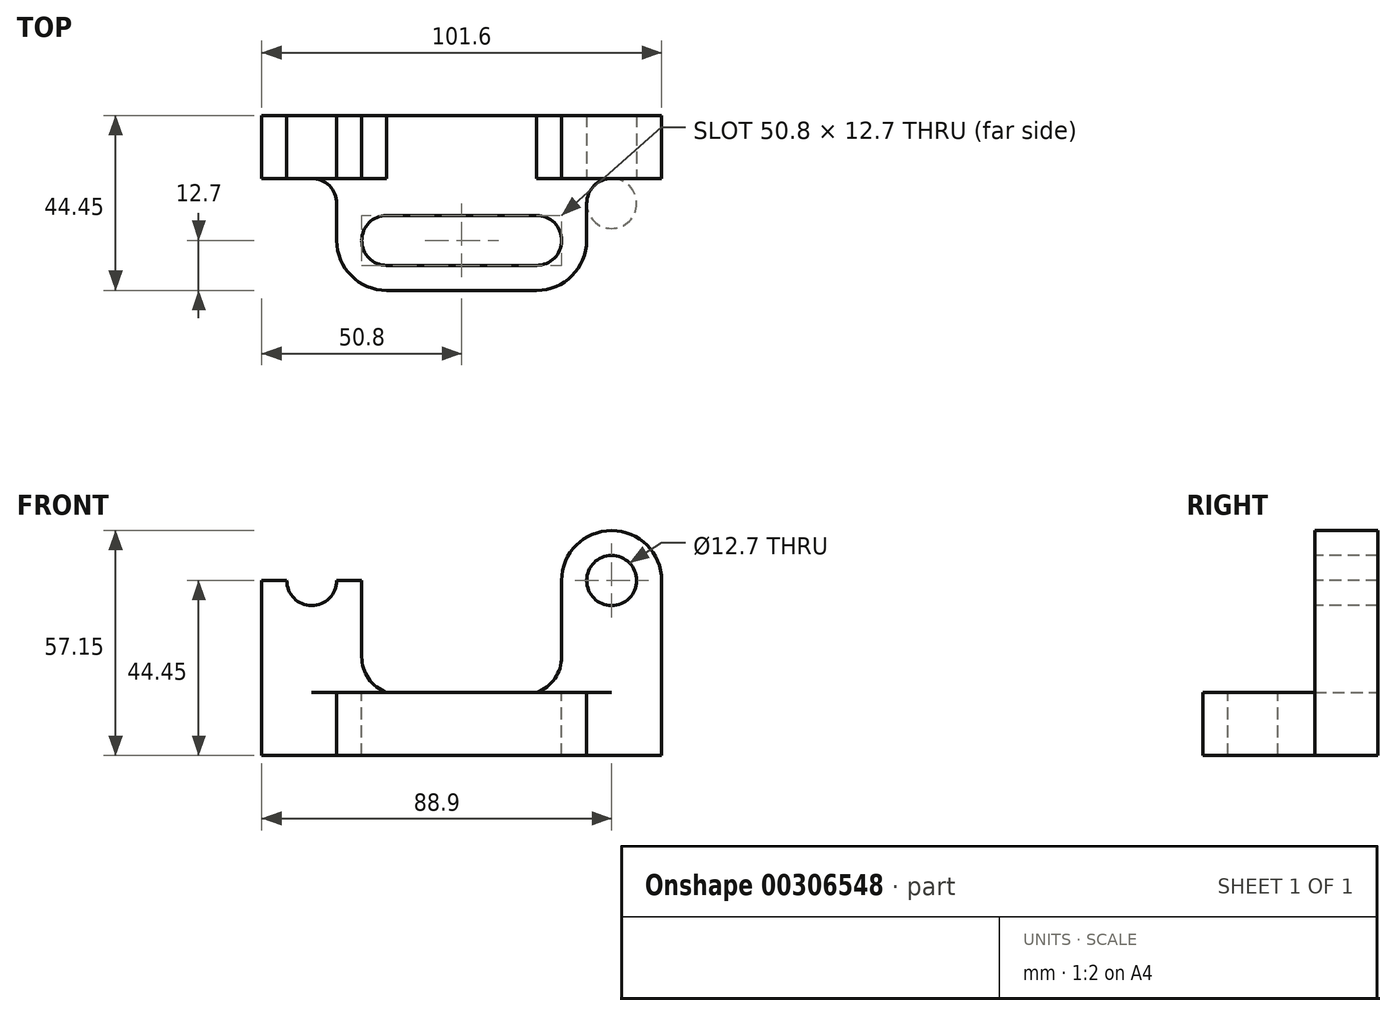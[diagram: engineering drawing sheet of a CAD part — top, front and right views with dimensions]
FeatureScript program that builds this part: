
annotation { "Feature Type Name" : "Feature", "Feature Type Description" : "" }
export const myFeature = defineFeature(function(context is Context, id is Id, definition is map)
    precondition{}
    {
        {
            var Q0;
            Q0=qCreatedBy(makeId("Front.planeOp"),FACE);
            var sketch = newSketch(context, id + "F0", { "sketchPlane" : qUnion([Q0])});
            skLineSegment(sketch, "E0", {"start": v(0, 0) * mm, "end": v(0, 44.45) * mm});
            skLineSegment(sketch, "E1", {"start": v(101.6, 44.45) * mm, "end": v(101.6, 0) * mm});
            skLineSegment(sketch, "E2", {"start": v(101.6, 0) * mm, "end": v(0, 0) * mm});
            skArc(sketch, "E3", {"start": v(0, 44.45) * mm, "mid": v(12.7, 57.15) * mm, "end": v(25.4, 44.45) * mm});
            skArc(sketch, "E4", {"start": v(101.6, 44.45) * mm, "mid": v(88.9, 57.15) * mm, "end": v(76.2, 44.45) * mm});
            skPoint(sketch, "E5.visualSharp", {"position": v(31.75, 16) * mm});
            skPoint(sketch, "E6.visualSharp", {"position": v(69.85, 16) * mm});
            skLineSegment(sketch, "E7", {"start": v(0, 44.45) * mm, "end": v(25.4, 44.45) * mm});
            skLineSegment(sketch, "E8", {"start": v(25.4, 25.07) * mm, "end": v(25.4, 44.45) * mm});
            skLineSegment(sketch, "E9", {"start": v(76.2, 44.45) * mm, "end": v(101.6, 44.45) * mm});
            skLineSegment(sketch, "E10", {"start": v(76.2, 44.45) * mm, "end": v(76.2, 25.07) * mm});
            skLineSegment(sketch, "E11", {"start": v(31.75, 16) * mm, "end": v(69.85, 16) * mm});
            skArc(sketch, "E12", {"start": v(25.4, 25.07) * mm, "mid": v(27.15, 19.54) * mm, "end": v(31.75, 16) * mm});
            skArc(sketch, "E13", {"start": v(76.2, 25.07) * mm, "mid": v(74.45, 19.54) * mm, "end": v(69.85, 16) * mm});
            skSolve(sketch);
        }
        {
            var Q0;
            Q0=makeQuery(id+"F0.imprint","IMPRINT",FACE,{"disambiguationData":[TD([[makeQuery(id+"F0.imprint","IMPRINT",EDGE,{"derivedFrom":sQuery(id+"F0.wireOp",EDGE,"E0")}),-1.0]])]});
            var Q1;
            Q1=makeQuery(id+"F0.imprint","IMPRINT",FACE,{"disambiguationData":[TD([[makeQuery(id+"F0.imprint","IMPRINT",EDGE,{"derivedFrom":sQuery(id+"F0.wireOp",EDGE,"C7aaIfA7-VipN-1Ud3-wAkr-EcyWhxY0K1Mf")}),1.0]])]});
            var Q2;
            Q2=makeQuery(id+"F0.imprint","IMPRINT",FACE,{"disambiguationData":[TD([[makeQuery(id+"F0.imprint","IMPRINT",EDGE,{"derivedFrom":sQuery(id+"F0.wireOp",EDGE,"wvJyilND-zbaq-GOeX-fCs7-xdRXK4oRubfT")}),1.0]])]});
            var Q3;
            Q3=makeQuery(id+"F0.imprint","IMPRINT",FACE,{"disambiguationData":[TD([[makeQuery(id+"F0.imprint","IMPRINT",EDGE,{"derivedFrom":sQuery(id+"F0.wireOp",EDGE,"E3")}),-1.0]])]});
            var Q4;
            Q4=makeQuery(id+"F0.imprint","IMPRINT",FACE,{"disambiguationData":[TD([[makeQuery(id+"F0.imprint","IMPRINT",EDGE,{"derivedFrom":sQuery(id+"F0.wireOp",EDGE,"E4")}),1.0]])]});
            extrude(context, id + "F1", {"entities" : qUnion([Q0, Q1, Q2, Q3, Q4]), "depth" : 16 * mm});
        }
        {
            var Q0;
            Q0=makeQuery(id+"F1.opExtrude","CAP_FACE",FACE,{"disambiguationData":[OSD([sQuery(id+"F0.wireOp",EDGE,"E0"),sQuery(id+"F0.wireOp",EDGE,"9CRlnIDt-vcet-FBRM-5pKB-gH7wcVJ6uEmm"),sQuery(id+"F0.wireOp",EDGE,"Mr6CpWdK-1kxF-I1DH-Dydn-HKWitOx3AbeL"),sQuery(id+"F0.wireOp",EDGE,"eOw6Qrws-JXzc-CHKK-sqTM-Dx20Xxl2jX9B"),sQuery(id+"F0.wireOp",EDGE,"E1"),sQuery(id+"F0.wireOp",EDGE,"E2"),sQuery(id+"F0.wireOp",EDGE,"E3"),sQuery(id+"F0.wireOp",EDGE,"E4"),sQuery(id+"F0.wireOp",EDGE,"E5.filletArc"),sQuery(id+"F0.wireOp",EDGE,"E6.filletArc")])],"isStart":false});
            var sketch = newSketch(context, id + "F2", { "sketchPlane" : qUnion([Q0])});
            skCircle(sketch, "E14", {"center": v(12.7, 44.45) * mm, "radius": 6.35 * mm});
            skCircle(sketch, "E15", {"center": v(88.9, 44.45) * mm, "radius": 6.35 * mm});
            skSolve(sketch);
        }
        {
            var Q0;
            Q0 = qSketchRegion(id + "F2", true);
            extrude(context, id + "F3", {"entities" : qUnion([Q0]), "operationType" : NewBodyOperationType.REMOVE, "endBound" : BoundingType.THROUGH_ALL, "oppositeDirection" : true, "depth" : 25.4 * mm});
        }
        {
            var Q0;
            Q0=makeQuery(id+"FVLnCp9fyohD2F4_1.boolean.opBoolean","MERGE",FACE,{"derivedFrom":[makeQuery(id+"F1.opExtrude","SWEPT_FACE",FACE,{"disambiguationData":[OSD([sQuery(id+"F0.wireOp",EDGE,"E11")])]}),makeQuery(id+"FVLnCp9fyohD2F4_1.opExtrude","CAP_FACE",FACE,{"disambiguationData":[OSD([sQuery(id+"FzZExjau3MCj1B7_1.wireOp",EDGE,"XOSryu3R-NVdj-X269-B07o-RXvqB5MkUpun.bottom"),sQuery(id+"FzZExjau3MCj1B7_1.wireOp",EDGE,"XOSryu3R-NVdj-X269-B07o-RXvqB5MkUpun.top"),sQuery(id+"FzZExjau3MCj1B7_1.wireOp",EDGE,"9fc3b264-000b-41c9-a5fc-efb56df5d0a9.filletArc"),sQuery(id+"FzZExjau3MCj1B7_1.wireOp",EDGE,"9b0ec235-3ef0-4ba8-8305-67645c6b1f3e.filletArc"),sQuery(id+"FzZExjau3MCj1B7_1.wireOp",EDGE,"mUgBNYwF-wCB2-l6hV-Al3r-JXlvUzJwsPNW"),sQuery(id+"FzZExjau3MCj1B7_1.wireOp",EDGE,"baKKjl0d-84Nd-DRWt-C5dw-ULHHoSTGuezj"),sQuery(id+"FzZExjau3MCj1B7_1.wireOp",EDGE,"Xwfjsm1I-eiXS-r64X-3sAk-xe5eMy7syard"),sQuery(id+"FzZExjau3MCj1B7_1.wireOp",EDGE,"VTm3dA6z-nvNZ-Ms79-g5wl-CRP6X4qjIYgN")])],"isStart":false})]});
            var sketch = newSketch(context, id + "F4", { "sketchPlane" : qUnion([Q0])});
            skLineSegment(sketch, "E16.bottom", {"start": v(31.75, -25.4) * mm, "end": v(69.85, -25.4) * mm});
            skLineSegment(sketch, "E16.top", {"start": v(31.75, -38.1) * mm, "end": v(69.85, -38.1) * mm});
            skLineSegment(sketch, "E16.left", {"start": v(31.75, -25.4) * mm, "end": v(31.75, -38.1) * mm});
            skLineSegment(sketch, "E16.right", {"start": v(69.85, -25.4) * mm, "end": v(69.85, -38.1) * mm});
            skArc(sketch, "E17", {"start": v(31.75, -25.4) * mm, "mid": v(25.4, -31.75) * mm, "end": v(31.75, -38.1) * mm});
            skArc(sketch, "E18", {"start": v(69.85, -38.1) * mm, "mid": v(76.2, -31.75) * mm, "end": v(69.85, -25.4) * mm});
            skSolve(sketch);
        }
        {
            var Q0;
            Q0=qCreatedBy(makeId("Top.planeOp"),FACE);
            var sketch = newSketch(context, id + "F5", { "sketchPlane" : qUnion([Q0])});
            skLineSegment(sketch, "E19", {"start": v(31.75, -44.45) * mm, "end": v(69.85, -44.45) * mm});
            skLineSegment(sketch, "E20", {"start": v(19.05, -22.35) * mm, "end": v(19.05, -31.75) * mm});
            skLineSegment(sketch, "E21", {"start": v(82.55, -22.35) * mm, "end": v(82.55, -31.75) * mm});
            skArc(sketch, "E22", {"start": v(19.05, -31.75) * mm, "mid": v(22.77, -40.73) * mm, "end": v(31.75, -44.45) * mm});
            skArc(sketch, "E23", {"start": v(69.85, -44.45) * mm, "mid": v(78.83, -40.73) * mm, "end": v(82.55, -31.75) * mm});
            skArc(sketch, "E24", {"start": v(82.55, -22.35) * mm, "mid": v(84.4, -17.86) * mm, "end": v(88.9, -16) * mm});
            skArc(sketch, "E25", {"start": v(19.05, -22.35) * mm, "mid": v(17.2, -17.86) * mm, "end": v(12.7, -16) * mm});
            skLineSegment(sketch, "E26", {"start": v(19.05, -22.35) * mm, "end": v(19.05, -16) * mm});
            skLineSegment(sketch, "E27", {"start": v(19.05, -16) * mm, "end": v(12.7, -16) * mm});
            skLineSegment(sketch, "E28", {"start": v(82.55, -22.35) * mm, "end": v(82.55, -16) * mm});
            skLineSegment(sketch, "E29", {"start": v(82.55, -16) * mm, "end": v(88.9, -16) * mm});
            skLineSegment(sketch, "E30", {"start": v(19.05, -16) * mm, "end": v(82.55, -16) * mm});
            skSolve(sketch);
        }
        {
            var Q0;
            Q0 = qSketchRegion(id + "F5", true);
            extrude(context, id + "F6", {"entities" : qUnion([Q0]), "operationType" : NewBodyOperationType.ADD, "depth" : 16 * mm});
        }
        {
            var Q0;
            Q0 = qSketchRegion(id + "F4", true);
            extrude(context, id + "F7", {"entities" : qUnion([Q0]), "operationType" : NewBodyOperationType.REMOVE, "endBound" : BoundingType.THROUGH_ALL, "oppositeDirection" : true, "depth" : 25.4 * mm});
        }
    });
